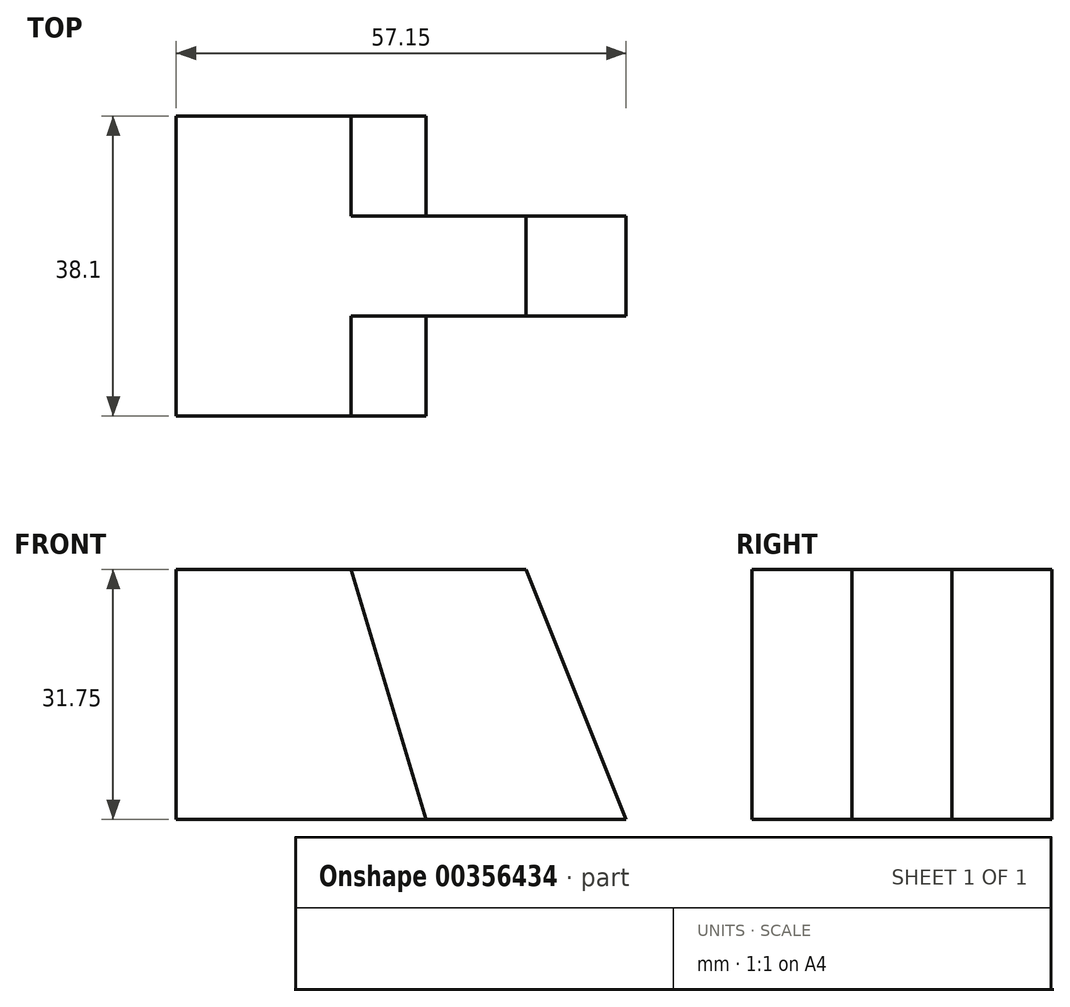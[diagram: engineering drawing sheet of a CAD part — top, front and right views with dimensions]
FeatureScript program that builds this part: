
annotation { "Feature Type Name" : "Feature", "Feature Type Description" : "" }
export const myFeature = defineFeature(function(context is Context, id is Id, definition is map)
    precondition{}
    {
        {
            var Q0;
            Q0=qCreatedBy(makeId("Front.planeOp"),FACE);
            var sketch = newSketch(context, id + "F0", { "sketchPlane" : qUnion([Q0])});
            skLineSegment(sketch, "E0", {"start": v(0, 31.75) * mm, "end": v(0, 0) * mm});
            skLineSegment(sketch, "E1", {"start": v(0, 0) * mm, "end": v(57.15, 0) * mm});
            skLineSegment(sketch, "E2", {"start": v(57.15, 0) * mm, "end": v(57.15, 31.75) * mm});
            skLineSegment(sketch, "E3", {"start": v(57.15, 31.75) * mm, "end": v(0, 31.75) * mm});
            skSolve(sketch);
        }
        {
            var Q0;
            Q0 = qSketchRegion(id + "F0", true);
            extrude(context, id + "F1", {"entities" : qUnion([Q0]), "depth" : 38.1 * mm});
        }
        {
            var Q0;
            Q0=makeQuery(id+"F1.opExtrude","CAP_FACE",FACE,{"disambiguationData":[OSD([sQuery(id+"F0.wireOp",EDGE,"E0"),sQuery(id+"F0.wireOp",EDGE,"E1"),sQuery(id+"F0.wireOp",EDGE,"E2"),sQuery(id+"F0.wireOp",EDGE,"E3")])],"isStart":false});
            var sketch = newSketch(context, id + "F2", { "sketchPlane" : qUnion([Q0])});
            skLineSegment(sketch, "E4", {"start": v(44.45, 31.75) * mm, "end": v(57.15, 0) * mm});
            skSolve(sketch);
        }
        {
            var Q0;
            Q0 = qSketchRegion(id + "F2", true);
            var Q1;
            {var subQ0=sQuery(id+"F2.wireOp",EDGE,"E4");Q1=makeQuery(id+"F2.imprint","IMPRINT",FACE,{"disambiguationData":[TD([[makeQuery(id+"F2.imprint","IMPRINT",EDGE,{"derivedFrom":subQ0}),1.0]])]});}
            extrude(context, id + "F3", {"entities" : qUnion([Q0, Q1]), "operationType" : NewBodyOperationType.REMOVE, "oppositeDirection" : true, "depth" : 38.1 * mm});
        }
        {
            var Q0;
            Q0=makeQuery(id+"F1.opExtrude","CAP_FACE",FACE,{"disambiguationData":[OSD([sQuery(id+"F0.wireOp",EDGE,"E0"),sQuery(id+"F0.wireOp",EDGE,"E1"),sQuery(id+"F0.wireOp",EDGE,"E2"),sQuery(id+"F0.wireOp",EDGE,"E3")])],"isStart":false});
            var sketch = newSketch(context, id + "F4", { "sketchPlane" : qUnion([Q0])});
            skLineSegment(sketch, "E5", {"start": v(22.22, 31.75) * mm, "end": v(31.75, 0) * mm});
            skSolve(sketch);
        }
        {
            var Q0;
            {var subQ0=sQuery(id+"F4.wireOp",EDGE,"E5");Q0=makeQuery(id+"F4.imprint","IMPRINT",FACE,{"disambiguationData":[TD([[makeQuery(id+"F4.imprint","IMPRINT",EDGE,{"derivedFrom":subQ0}),1.0]])]});}
            extrude(context, id + "F5", {"entities" : qUnion([Q0]), "operationType" : NewBodyOperationType.REMOVE, "oppositeDirection" : true, "depth" : 12.7 * mm});
        }
        {
            var Q0;
            Q0=makeQuery(id+"F1.opExtrude","CAP_FACE",FACE,{"disambiguationData":[OSD([sQuery(id+"F0.wireOp",EDGE,"E0"),sQuery(id+"F0.wireOp",EDGE,"E1"),sQuery(id+"F0.wireOp",EDGE,"E2"),sQuery(id+"F0.wireOp",EDGE,"E3")])],"isStart":true});
            var sketch = newSketch(context, id + "F6", { "sketchPlane" : qUnion([Q0])});
            skLineSegment(sketch, "E6", {"start": v(-31.75, 0) * mm, "end": v(-22.22, 31.75) * mm});
            skSolve(sketch);
        }
        {
            var Q0;
            Q0 = qSketchRegion(id + "F6", true);
            var Q1;
            {var subQ0=sQuery(id+"F6.wireOp",EDGE,"E6");Q1=makeQuery(id+"F6.imprint","IMPRINT",FACE,{"disambiguationData":[TD([[makeQuery(id+"F6.imprint","IMPRINT",EDGE,{"derivedFrom":subQ0}),1.0]])]});}
            extrude(context, id + "F7", {"entities" : qUnion([Q0, Q1]), "operationType" : NewBodyOperationType.REMOVE, "oppositeDirection" : true, "depth" : 12.7 * mm});
        }
    });
